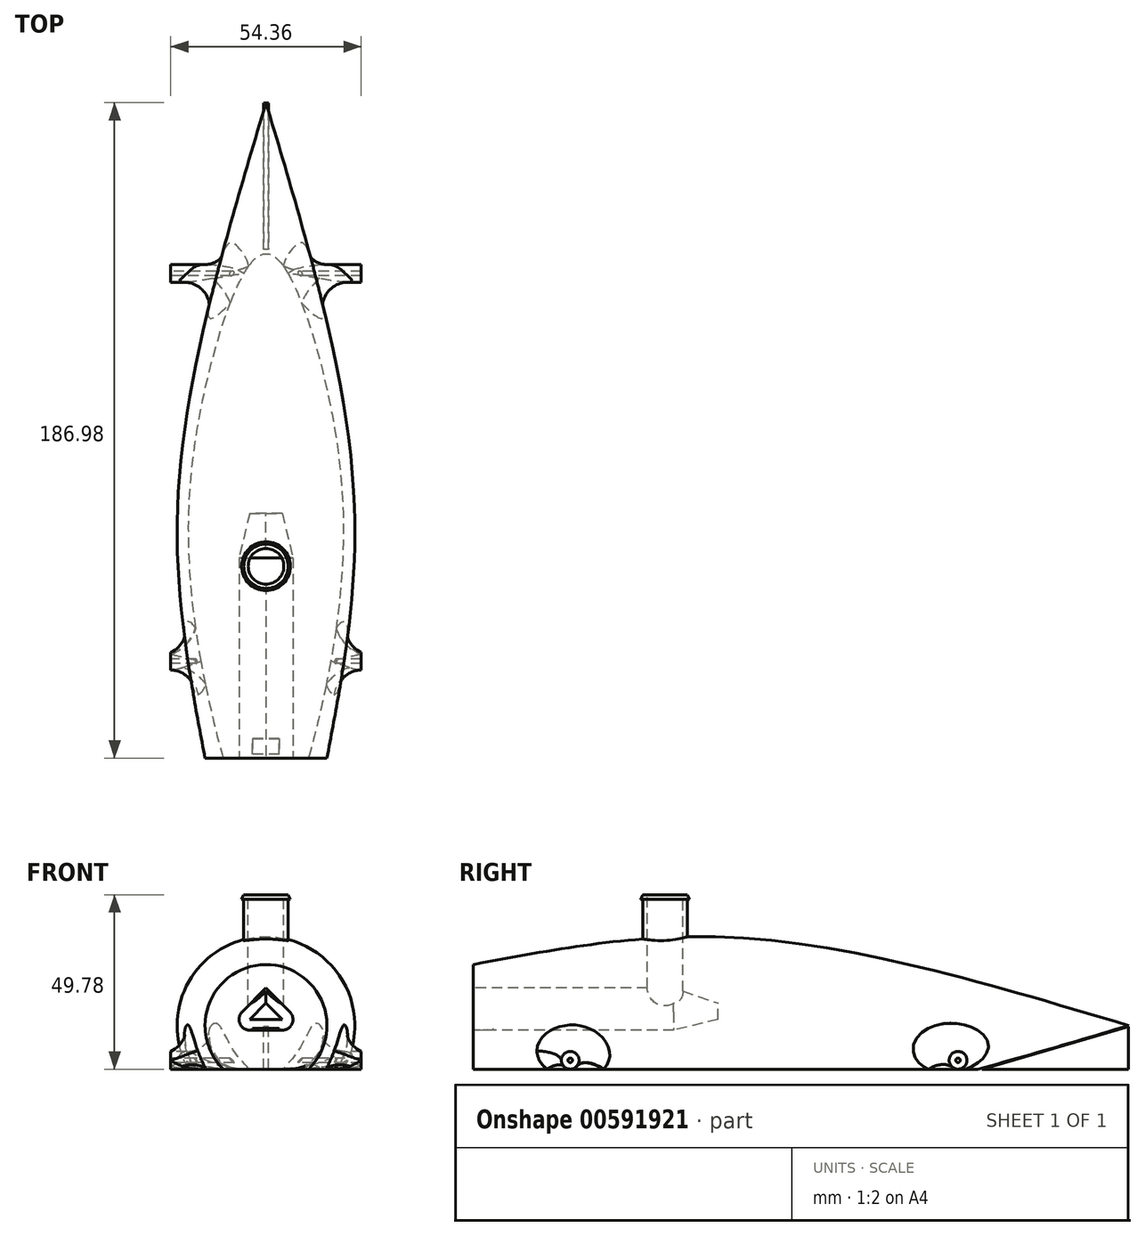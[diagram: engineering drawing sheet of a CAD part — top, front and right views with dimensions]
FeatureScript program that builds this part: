
annotation { "Feature Type Name" : "Feature", "Feature Type Description" : "" }
export const myFeature = defineFeature(function(context is Context, id is Id, definition is map)
    precondition{}
    {
        {
            var Q0;
            Q0=qCreatedBy(makeId("Top.planeOp"),FACE);
            cPlane(context, id + "F0", {"entities" : qUnion([Q0]), "cplaneType" : CPlaneType.OFFSET, "offset" : 7.37 * mm, "width" : 152.4 * mm, "height" : 152.4 * mm});
        }
        {
            var Q0;
            Q0=qCreatedBy(makeId("Front.planeOp"),FACE);
            cPlane(context, id + "F1", {"entities" : qUnion([Q0]), "cplaneType" : CPlaneType.OFFSET, "offset" : 99.82 * mm, "width" : 152.4 * mm, "height" : 152.4 * mm});
        }
        {
            var Q0;
            Q0=qCreatedBy(id+"F0.planeOp",FACE);
            var sketch = newSketch(context, id + "F2", { "sketchPlane" : qUnion([Q0])});
            skLineSegment(sketch, "E0", {"start": v(0, -99.9) * mm, "end": v(-17.4, -99.9) * mm});
            skFitSpline(sketch, "E1", {"points": [v(-17.4, -99.9) * mm, v(-24.98, -23.09) * mm, v(0, 87.08) * mm], "startDerivative": vector(-30.87, 162.6) * mm, "endDerivative": vector(62.7, 209.85) * mm});
            skLineSegment(sketch, "E2", {"start": v(0, -99.9) * mm, "end": v(0, 87.08) * mm});
            skSolve(sketch);
        }
        {
            var Q0;
            Q0 = qSketchRegion(id + "F2", true);
            var Q1;
            Q1=sQuery(id+"F2.wireOp",EDGE,"E2");
            revolve(context, id + "F3", {"entities" : qUnion([Q0]), "axis" : qUnion([Q1]), "revolveType" : RevolveType.FULL});
        }
        {
            var Q0;
            Q0=makeQuery(id+"F3.opRevolve","SWEPT_FACE",FACE,{"disambiguationData":[OSD([sQuery(id+"F2.wireOp",EDGE,"E0")])]});
            var sketch = newSketch(context, id + "F4", { "sketchPlane" : qUnion([Q0])});
            skLineSegment(sketch, "E3", {"start": v(0, 18.06) * mm, "end": v(-6.8, 11.25) * mm});
            skLineSegment(sketch, "E4", {"start": v(-4.65, 6.05) * mm, "end": v(0, 6.05) * mm});
            skLineSegment(sketch, "E5", {"start": v(0, 18.06) * mm, "end": v(6.8, 11.25) * mm});
            skLineSegment(sketch, "E6", {"start": v(4.65, 6.05) * mm, "end": v(0, 6.05) * mm});
            skArc(sketch, "E7", {"start": v(-6.8, 11.25) * mm, "mid": v(-7.47, 7.93) * mm, "end": v(-4.65, 6.05) * mm});
            skArc(sketch, "E8", {"start": v(4.65, 6.05) * mm, "mid": v(7.47, 7.93) * mm, "end": v(6.8, 11.25) * mm});
            skSolve(sketch);
        }
        {
            var Q0;
            Q0=qSketchRegion(id+"F4",true);
            extrude(context, id + "F5", {"entities" : qUnion([Q0]), "operationType" : NewBodyOperationType.REMOVE, "oppositeDirection" : true, "depth" : 69.85 * mm, "offsetDistance" : 25.4 * mm});
        }
        {
            var Q0;
            Q0=qCreatedBy(makeId("Right.planeOp"),FACE);
            var sketch = newSketch(context, id + "F6", { "sketchPlane" : qUnion([Q0])});
            skLineSegment(sketch, "E9", {"start": v(-38.84, 24.35) * mm, "end": v(-38.84, 43.4) * mm});
            skLineSegment(sketch, "E10", {"start": v(-38.84, 43.4) * mm, "end": v(-38.22, 43.4) * mm});
            skLineSegment(sketch, "E11", {"start": v(-38.22, 43.4) * mm, "end": v(-38.84, 44.7) * mm});
            skLineSegment(sketch, "E12", {"start": v(-38.84, 44.7) * mm, "end": v(-45.19, 44.7) * mm});
            skLineSegment(sketch, "E13", {"start": v(-45.19, 44.7) * mm, "end": v(-45.19, 24.35) * mm});
            skLineSegment(sketch, "E14", {"start": v(-38.84, 24.35) * mm, "end": v(-45.19, 24.35) * mm});
            skSolve(sketch);
        }
        {
            var Q0;
            Q0=qSketchRegion(id+"F6",true);
            var Q1;
            Q1=sQuery(id+"F6.wireOp",EDGE,"E13");
            revolve(context, id + "F7", {"operationType" : NewBodyOperationType.ADD, "entities" : qUnion([Q0]), "axis" : qUnion([Q1]), "revolveType" : RevolveType.FULL});
        }
        {
            var Q0;
            Q0=makeQuery(id+"F7.opRevolve","SWEPT_FACE",FACE,{"disambiguationData":[OSD([sQuery(id+"F6.wireOp",EDGE,"E12")])]});
            var sketch = newSketch(context, id + "F8", { "sketchPlane" : qUnion([Q0])});
            skCircle(sketch, "E15", {"center": v(0, -45.19) * mm, "radius": 5.08 * mm});
            skSolve(sketch);
        }
        {
            var Q0;
            Q0=qSketchRegion(id+"F8",true);
            extrude(context, id + "F9", {"entities" : qUnion([Q0]), "operationType" : NewBodyOperationType.REMOVE, "oppositeDirection" : true, "depth" : 32.77 * mm, "offsetDistance" : 25.4 * mm});
        }
        {
            var Q0;
            Q0=qCreatedBy(makeId("Top.planeOp"),FACE);
            cPlane(context, id + "F10", {"entities" : qUnion([Q0]), "cplaneType" : CPlaneType.OFFSET, "offset" : 5.08 * mm, "oppositeDirection" : true, "width" : 152.4 * mm, "height" : 152.4 * mm});
        }
        {
            var Q0;
            Q0=qCreatedBy(id+"F10.planeOp",FACE);
            var sketch = newSketch(context, id + "F11", { "sketchPlane" : qUnion([Q0])});
            skLineSegment(sketch, "E16.bottom", {"start": v(73.32, 143.23) * mm, "end": v(-63.31, 143.23) * mm});
            skLineSegment(sketch, "E16.top", {"start": v(73.32, -152.23) * mm, "end": v(-63.31, -152.23) * mm});
            skLineSegment(sketch, "E16.left", {"start": v(73.32, 143.23) * mm, "end": v(73.32, -152.23) * mm});
            skLineSegment(sketch, "E16.right", {"start": v(-63.31, 143.23) * mm, "end": v(-63.31, -152.23) * mm});
            skSolve(sketch);
        }
        {
            var Q0;
            Q0 = qSketchRegion(id + "F11", true);
            extrude(context, id + "F12", {"entities" : qUnion([Q0]), "operationType" : NewBodyOperationType.REMOVE, "oppositeDirection" : true, "depth" : 25.4 * mm, "offsetDistance" : 25.4 * mm});
        }
        {
            var Q0;
            Q0=makeQuery(id+"F5.boolean.opBoolean","COPY",EDGE,{"derivedFrom":makeQuery(id+"F5.opExtrude","CAP_EDGE",EDGE,{"disambiguationData":[OSD([sQuery(id+"F4.wireOp",EDGE,"E3")])],"isStart":false})});
            chamfer(context, id + "F13", {"entities" : qUnion([Q0]), "chamferType" : ChamferType.TWO_OFFSETS, "width1" : 3.05 * mm, "oppositeDirection" : false, "width2" : 12.7 * mm, "tangentPropagation" : true});
        }
        {
            var Q0;
            Q0=qCreatedBy(makeId("Right.planeOp"),FACE);
            var sketch = newSketch(context, id + "F14", { "sketchPlane" : qUnion([Q0])});
            skLineSegment(sketch, "E17", {"start": v(45.18, -5.08) * mm, "end": v(87.03, 7.1) * mm});
            skLineSegment(sketch, "E18", {"start": v(87.03, 7.1) * mm, "end": v(87.03, -5.08) * mm});
            skLineSegment(sketch, "E19", {"start": v(87.03, -5.08) * mm, "end": v(45.18, -5.08) * mm});
            skSolve(sketch);
        }
        {
            var Q0;
            Q0 = qSketchRegion(id + "F14", true);
            extrude(context, id + "F15", {"entities" : qUnion([Q0]), "endBound" : BoundingType.SYMMETRIC, "depth" : 1.42 * mm, "offsetDistance" : 25.4 * mm});
        }
        {
            var Q0;
            Q0=qCreatedBy(makeId("Right.planeOp"),FACE);
            var sketch = newSketch(context, id + "F16", { "sketchPlane" : qUnion([Q0])});
            skCircle(sketch, "E20", {"center": v(38.4, -2.54) * mm, "radius": 2.54 * mm});
            skCircle(sketch, "E21", {"center": v(38.4, -2.54) * mm, "radius": 0.64 * mm});
            skCircle(sketch, "E22", {"center": v(-72.27, -2.54) * mm, "radius": 2.54 * mm});
            skCircle(sketch, "E23", {"center": v(-72.27, -2.54) * mm, "radius": 0.64 * mm});
            skSolve(sketch);
        }
        {
            var Q0;
            Q0 = qSketchRegion(id + "F16", true);
            extrude(context, id + "F17", {"entities" : qUnion([Q0]), "operationType" : NewBodyOperationType.ADD, "endBound" : BoundingType.SYMMETRIC, "depth" : 54.36 * mm, "offsetDistance" : 25.4 * mm});
        }
        {
            var Q0;
            Q0=makeQuery(id+"F17.boolean.opBoolean","INTERSECT",EDGE,{"disambiguationData":[OD(0.0)],"derivedFrom":[makeQuery(id+"F3.opRevolve","SWEPT_FACE",FACE,{"disambiguationData":[OSD([sQuery(id+"F2.wireOp",EDGE,"E1")])]}),makeQuery(id+"F17.opExtrude","SWEPT_FACE",FACE,{"disambiguationData":[OSD([sQuery(id+"F16.wireOp",EDGE,"E20")])]})]});
            var Q1;
            Q1=makeQuery(id+"F17.boolean.opBoolean","INTERSECT",EDGE,{"disambiguationData":[OD(1.0)],"derivedFrom":[makeQuery(id+"F3.opRevolve","SWEPT_FACE",FACE,{"disambiguationData":[OSD([sQuery(id+"F2.wireOp",EDGE,"E1")])]}),makeQuery(id+"F17.opExtrude","SWEPT_FACE",FACE,{"disambiguationData":[OSD([sQuery(id+"F16.wireOp",EDGE,"E20")])]})]});
            var Q2;
            Q2=makeQuery(id+"F17.boolean.opBoolean","INTERSECT",EDGE,{"disambiguationData":[OD(0.0)],"derivedFrom":[makeQuery(id+"F3.opRevolve","SWEPT_FACE",FACE,{"disambiguationData":[OSD([sQuery(id+"F2.wireOp",EDGE,"E1")])]}),makeQuery(id+"F17.opExtrude","SWEPT_FACE",FACE,{"disambiguationData":[OSD([sQuery(id+"F16.wireOp",EDGE,"E22")])]})]});
            var Q3;
            Q3=makeQuery(id+"F17.boolean.opBoolean","INTERSECT",EDGE,{"disambiguationData":[OD(1.0)],"derivedFrom":[makeQuery(id+"F3.opRevolve","SWEPT_FACE",FACE,{"disambiguationData":[OSD([sQuery(id+"F2.wireOp",EDGE,"E1")])]}),makeQuery(id+"F17.opExtrude","SWEPT_FACE",FACE,{"disambiguationData":[OSD([sQuery(id+"F16.wireOp",EDGE,"E22")])]})]});
            fillet(context, id + "F18", {"entities" : qUnion([Q0, Q1, Q2, Q3]), "radius" : 8.38 * mm, "tangentPropagation" : true, "allowEdgeOverflow" : false});
        }
        {
            var Q0;
            Q0=qCreatedBy(makeId("Right.planeOp"),FACE);
            var sketch = newSketch(context, id + "F19", { "sketchPlane" : qUnion([Q0])});
            skLineSegment(sketch, "E24", {"start": v(-99.72, 5.95) * mm, "end": v(-94.4, 6.5) * mm});
            skLineSegment(sketch, "E25", {"start": v(-94.4, 6.5) * mm, "end": v(-94.3, 5.92) * mm});
            skLineSegment(sketch, "E26", {"start": v(-94.3, 5.92) * mm, "end": v(-99.72, 5.95) * mm});
            skSolve(sketch);
        }
        {
            var Q0;
            Q0 = qSketchRegion(id + "F19", true);
            extrude(context, id + "F20", {"entities" : qUnion([Q0]), "operationType" : NewBodyOperationType.ADD, "endBound" : BoundingType.SYMMETRIC, "depth" : 7.62 * mm, "offsetDistance" : 25.4 * mm});
        }
    });
